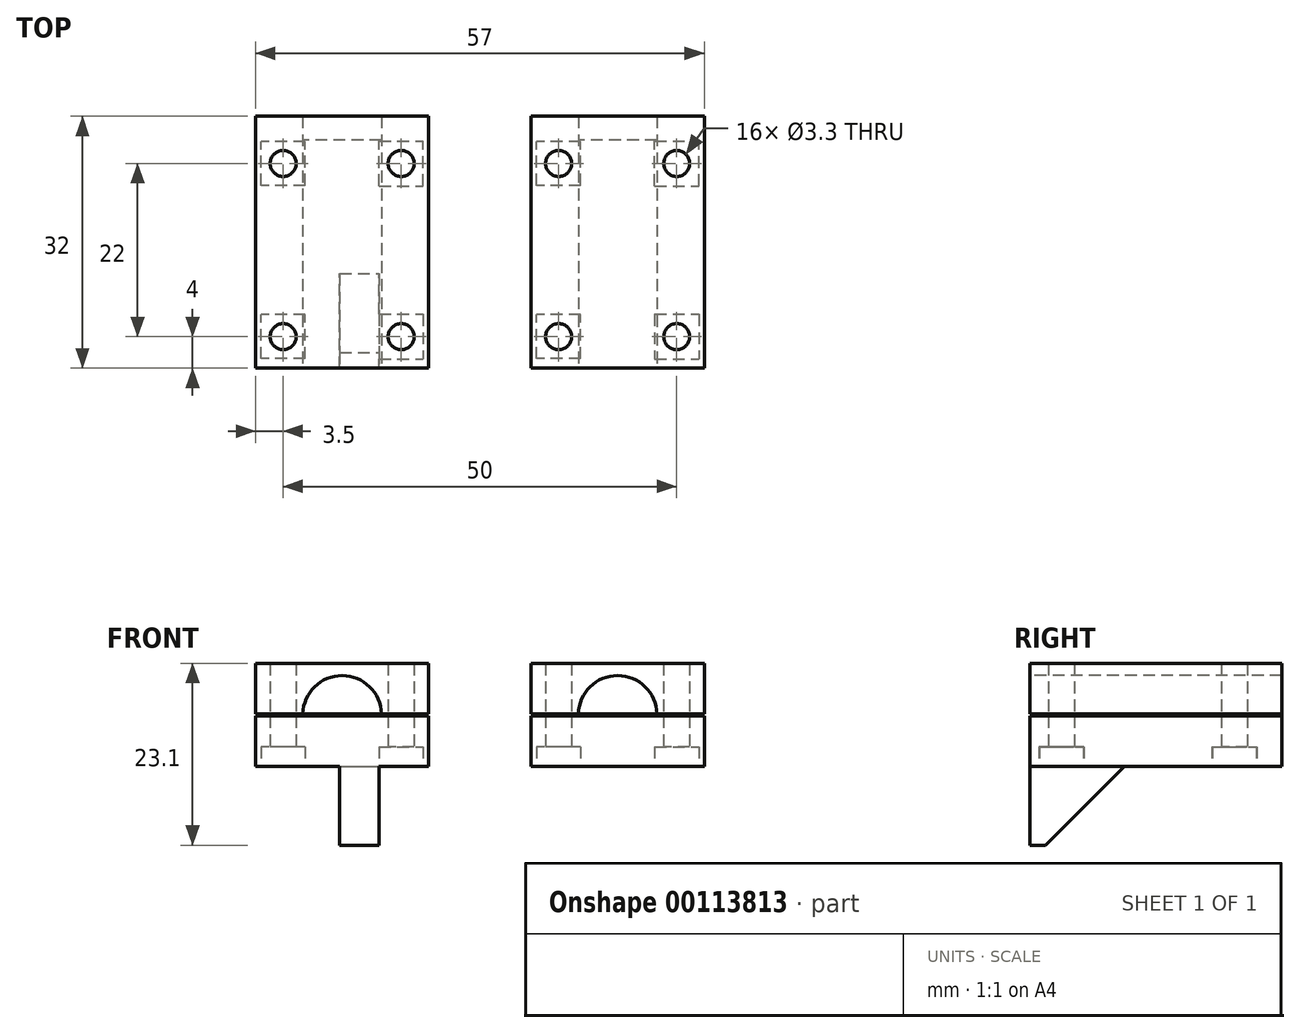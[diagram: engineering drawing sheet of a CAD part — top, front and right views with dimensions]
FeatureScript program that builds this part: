
annotation { "Feature Type Name" : "Feature", "Feature Type Description" : "" }
export const myFeature = defineFeature(function(context is Context, id is Id, definition is map)
    precondition{}
    {
        {
            var Q0;
            Q0=qCreatedBy(makeId("Top.planeOp"),FACE);
            var sketch = newSketch(context, id + "F0", { "sketchPlane" : qUnion([Q0])});
            skLineSegment(sketch, "E0.bottom", {"start": v(0, 0) * mm, "end": v(22, 0) * mm});
            skLineSegment(sketch, "E0.top", {"start": v(0, -32) * mm, "end": v(22, -32) * mm});
            skLineSegment(sketch, "E0.left", {"start": v(0, 0) * mm, "end": v(0, -32) * mm});
            skLineSegment(sketch, "E0.right", {"start": v(22, 0) * mm, "end": v(22, -32) * mm});
            skPoint(sketch, "E1", {"position": v(3.5, -28) * mm});
            skPoint(sketch, "E2", {"position": v(18.5, -28) * mm});
            skPoint(sketch, "E3", {"position": v(18.5, -6) * mm});
            skPoint(sketch, "E4", {"position": v(3.5, -6) * mm});
            skLineSegment(sketch, "E5", {"start": v(11, 0) * mm, "end": v(11, -32) * mm, "construction": true});
            skLineSegment(sketch, "E6.bottom", {"start": v(6.3, -8.8) * mm, "end": v(0.7, -8.8) * mm});
            skLineSegment(sketch, "E6.top", {"start": v(6.3, -3.2) * mm, "end": v(0.7, -3.2) * mm});
            skLineSegment(sketch, "E6.left", {"start": v(6.3, -8.8) * mm, "end": v(6.3, -3.2) * mm});
            skLineSegment(sketch, "E6.right", {"start": v(0.7, -8.8) * mm, "end": v(0.7, -3.2) * mm});
            skLineSegment(sketch, "E7.bottom", {"start": v(6.3, -30.8) * mm, "end": v(0.7, -30.8) * mm});
            skLineSegment(sketch, "E7.top", {"start": v(6.3, -25.2) * mm, "end": v(0.7, -25.2) * mm});
            skLineSegment(sketch, "E7.left", {"start": v(6.3, -30.8) * mm, "end": v(6.3, -25.2) * mm});
            skLineSegment(sketch, "E7.right", {"start": v(0.7, -30.8) * mm, "end": v(0.7, -25.2) * mm});
            skLineSegment(sketch, "E8.bottom", {"start": v(15.7, -25.14) * mm, "end": v(21.3, -25.14) * mm});
            skLineSegment(sketch, "E8.top", {"start": v(15.7, -30.86) * mm, "end": v(21.3, -30.86) * mm});
            skLineSegment(sketch, "E8.left", {"start": v(15.7, -25.14) * mm, "end": v(15.7, -30.86) * mm});
            skLineSegment(sketch, "E8.right", {"start": v(21.3, -25.14) * mm, "end": v(21.3, -30.86) * mm});
            skLineSegment(sketch, "E9.bottom", {"start": v(15.7, -8.86) * mm, "end": v(21.3, -8.86) * mm});
            skLineSegment(sketch, "E9.top", {"start": v(15.7, -3.14) * mm, "end": v(21.3, -3.14) * mm});
            skLineSegment(sketch, "E9.left", {"start": v(15.7, -8.86) * mm, "end": v(15.7, -3.14) * mm});
            skLineSegment(sketch, "E9.right", {"start": v(21.3, -8.86) * mm, "end": v(21.3, -3.14) * mm});
            skSolve(sketch);
        }
        {
            var Q0;
            Q0 = qSketchRegion(id + "F0", true);
            var Q1;
            Q1=makeQuery(id+"F0.imprint","IMPRINT",FACE,{"disambiguationData":[TD([[makeQuery(id+"F0.imprint","IMPRINT",EDGE,{"derivedFrom":sQuery(id+"F0.wireOp",EDGE,"E6.bottom")}),-1.0]])]});
            var Q2;
            Q2=makeQuery(id+"F0.imprint","IMPRINT",FACE,{"disambiguationData":[TD([[makeQuery(id+"F0.imprint","IMPRINT",EDGE,{"derivedFrom":sQuery(id+"F0.wireOp",EDGE,"E9.bottom")}),1.0]])]});
            var Q3;
            Q3=makeQuery(id+"F0.imprint","IMPRINT",FACE,{"disambiguationData":[TD([[makeQuery(id+"F0.imprint","IMPRINT",EDGE,{"derivedFrom":sQuery(id+"F0.wireOp",EDGE,"E8.bottom")}),-1.0]])]});
            var Q4;
            Q4=makeQuery(id+"F0.imprint","IMPRINT",FACE,{"disambiguationData":[TD([[makeQuery(id+"F0.imprint","IMPRINT",EDGE,{"derivedFrom":sQuery(id+"F0.wireOp",EDGE,"E7.bottom")}),-1.0]])]});
            extrude(context, id + "F1", {"entities" : qUnion([Q0, Q1, Q2, Q3, Q4]), "depth" : 13.1 * mm});
        }
        {
            var Q0;
            Q0=makeQuery(id+"F0.imprint","IMPRINT",FACE,{"disambiguationData":[TD([[makeQuery(id+"F0.imprint","IMPRINT",EDGE,{"derivedFrom":sQuery(id+"F0.wireOp",EDGE,"E7.bottom")}),-1.0]])]});
            var Q1;
            Q1=makeQuery(id+"F0.imprint","IMPRINT",FACE,{"disambiguationData":[TD([[makeQuery(id+"F0.imprint","IMPRINT",EDGE,{"derivedFrom":sQuery(id+"F0.wireOp",EDGE,"E8.bottom")}),-1.0]])]});
            var Q2;
            Q2=makeQuery(id+"F0.imprint","IMPRINT",FACE,{"disambiguationData":[TD([[makeQuery(id+"F0.imprint","IMPRINT",EDGE,{"derivedFrom":sQuery(id+"F0.wireOp",EDGE,"E6.bottom")}),-1.0]])]});
            var Q3;
            Q3=makeQuery(id+"F0.imprint","IMPRINT",FACE,{"disambiguationData":[TD([[makeQuery(id+"F0.imprint","IMPRINT",EDGE,{"derivedFrom":sQuery(id+"F0.wireOp",EDGE,"E9.bottom")}),1.0]])]});
            extrude(context, id + "F2", {"entities" : qUnion([Q0, Q1, Q2, Q3]), "operationType" : NewBodyOperationType.REMOVE, "depth" : 2.5 * mm});
        }
        {
            var Q0;
            Q0=sQuery(id+"F0.wireOp",VERTEX,"E1");
            var Q1;
            Q1=sQuery(id+"F0.wireOp",VERTEX,"E2");
            var Q2;
            Q2=sQuery(id+"F0.wireOp",VERTEX,"E3");
            var Q3;
            Q3=sQuery(id+"F0.wireOp",VERTEX,"E4");
            var Q4;
            Q4=makeQuery(id+"F1.opExtrude","SWEPT_BODY",BODY,{"disambiguationData":[OSD([sQuery(id+"F0.wireOp",EDGE,"E0.bottom"),sQuery(id+"F0.wireOp",EDGE,"E0.top"),sQuery(id+"F0.wireOp",EDGE,"E0.left"),sQuery(id+"F0.wireOp",EDGE,"E0.right")])]});
            hole(context, id + "F3", {"style" : HoleStyle.SIMPLE, "endStyle" : HoleEndStyle.THROUGH, "oppositeDirection" : true, "holeDiameter" : 3.3 * mm, "startFromSketch" : true, "locations" : qUnion([Q0, Q1, Q2, Q3]), "scope" : qUnion([Q4]), "isTappedThrough" : true});
        }
        {
            var Q0;
            Q0=makeQuery(id+"F1.opExtrude","SWEPT_FACE",FACE,{"disambiguationData":[OSD([sQuery(id+"F0.wireOp",EDGE,"E0.top")])]});
            var sketch = newSketch(context, id + "F4", { "sketchPlane" : qUnion([Q0])});
            skLineSegment(sketch, "E10", {"start": v(11, 13.1) * mm, "end": v(11, 0) * mm, "construction": true});
            skLineSegment(sketch, "E11", {"start": v(0, 6.55) * mm, "end": v(22, 6.55) * mm, "construction": true});
            skPoint(sketch, "E12", {"position": v(11, 6.55) * mm});
            skCircle(sketch, "E13", {"center": v(11, 6.55) * mm, "radius": 5 * mm});
            skLineSegment(sketch, "E14.bottom", {"start": v(22, 6.4) * mm, "end": v(0, 6.4) * mm});
            skLineSegment(sketch, "E14.top", {"start": v(22, 6.7) * mm, "end": v(0, 6.7) * mm});
            skLineSegment(sketch, "E14.left", {"start": v(22, 6.4) * mm, "end": v(22, 6.7) * mm});
            skLineSegment(sketch, "E14.right", {"start": v(0, 6.4) * mm, "end": v(0, 6.7) * mm});
            skSolve(sketch);
        }
        {
            var Q0;
            Q0=makeQuery(id+"F4.imprint","IMPRINT",FACE,{"disambiguationData":[TD([[makeQuery(id+"F4.imprint","IMPRINT",EDGE,{"derivedFrom":sQuery(id+"F4.wireOp",EDGE,"E13")}),1.0]])]});
            var Q1;
            {var subQ0=sQuery(id+"F4.wireOp",EDGE,"E14.top");var subQ1=sQuery(id+"F4.wireOp",EDGE,"E13");var subQ2=makeQuery(id+"F4.imprint","INTERSECT",VERTEX,{"disambiguationData":[OD(0.0)],"derivedFrom":[subQ1,subQ0]});Q1=makeQuery(id+"F4.imprint","IMPRINT",FACE,{"disambiguationData":[TD([[makeQuery(id+"F4.imprint","IMPRINT",EDGE,{"disambiguationData":[TD([[subQ2,1.0]])],"derivedFrom":subQ1}),1.0]])]});}
            var Q2;
            {var subQ0=sQuery(id+"F4.wireOp",EDGE,"E14.bottom");var subQ1=sQuery(id+"F4.wireOp",EDGE,"E13");var subQ2=makeQuery(id+"F4.imprint","INTERSECT",VERTEX,{"disambiguationData":[OD(0.0)],"derivedFrom":[subQ1,subQ0]});Q2=makeQuery(id+"F4.imprint","IMPRINT",FACE,{"disambiguationData":[TD([[makeQuery(id+"F4.imprint","IMPRINT",EDGE,{"disambiguationData":[TD([[subQ2,-1.0]])],"derivedFrom":subQ1}),1.0]])]});}
            extrude(context, id + "F5", {"entities" : qUnion([Q0, Q1, Q2]), "operationType" : NewBodyOperationType.REMOVE, "oppositeDirection" : true, "depth" : 29 * mm});
        }
        {
            var Q0;
            {var subQ5=sQuery(id+"F4.wireOp",EDGE,"E14.right");Q0=makeQuery(id+"F4.imprint","IMPRINT",FACE,{"disambiguationData":[TD([[makeQuery(id+"F4.imprint","IMPRINT",EDGE,{"derivedFrom":subQ5}),1.0]])]});}
            var Q1;
            {var subQ5=sQuery(id+"F4.wireOp",EDGE,"E14.left");Q1=makeQuery(id+"F4.imprint","IMPRINT",FACE,{"disambiguationData":[TD([[makeQuery(id+"F4.imprint","IMPRINT",EDGE,{"derivedFrom":subQ5}),-1.0]])]});}
            var Q2;
            {var subQ0=sQuery(id+"F4.wireOp",EDGE,"E14.top");var subQ1=sQuery(id+"F4.wireOp",EDGE,"E13");var subQ2=makeQuery(id+"F4.imprint","INTERSECT",VERTEX,{"disambiguationData":[OD(0.0)],"derivedFrom":[subQ1,subQ0]});Q2=makeQuery(id+"F4.imprint","IMPRINT",FACE,{"disambiguationData":[TD([[makeQuery(id+"F4.imprint","IMPRINT",EDGE,{"disambiguationData":[TD([[subQ2,-1.0]])],"derivedFrom":subQ1}),1.0]])]});}
            extrude(context, id + "F6", {"entities" : qUnion([Q0, Q1, Q2]), "operationType" : NewBodyOperationType.REMOVE, "endBound" : BoundingType.THROUGH_ALL, "oppositeDirection" : true, "depth" : 25 * mm});
        }
        {
            var Q0;
            Q0=makeQuery(id+"F6.boolean.opBoolean","SPLIT",BODY,{"disambiguationData":[OD(0.0)],"derivedFrom":makeQuery(id+"F1.opExtrude","SWEPT_BODY",BODY,{"disambiguationData":[OSD([sQuery(id+"F0.wireOp",EDGE,"E0.bottom"),sQuery(id+"F0.wireOp",EDGE,"E0.top"),sQuery(id+"F0.wireOp",EDGE,"E0.left"),sQuery(id+"F0.wireOp",EDGE,"E0.right")])]})});
            transform(context, id + "F7", {"entities" : qUnion([Q0]), "transformType" : TransformType.TRANSLATION_3D, "dx" : -35 * mm, "dy" : 0 * mm, "dz" : 0 * mm, "makeCopy" : true});
        }
        {
            var Q0;
            Q0=makeQuery(id+"F7.opPattern","COPY",FACE,{"derivedFrom":makeQuery(id+"F2.boolean.opBoolean","COPY",FACE,{"derivedFrom":makeQuery(id+"F2.opExtrude","SWEPT_FACE",FACE,{"disambiguationData":[OSD([sQuery(id+"F0.wireOp",EDGE,"E8.left")])]})}),"instanceName":"1"});
            var sketch = newSketch(context, id + "F8", { "sketchPlane" : qUnion([Q0])});
            skLineSegment(sketch, "E15.0", {"start": v(-25.14, 0) * mm, "end": v(-30.86, 0) * mm});
            skPoint(sketch, "E16.0", {"position": v(-32, 0) * mm});
            skLineSegment(sketch, "E17", {"start": v(-32, 0) * mm, "end": v(-20, 0) * mm});
            skLineSegment(sketch, "E18", {"start": v(-20, 0) * mm, "end": v(-30, -10) * mm});
            skLineSegment(sketch, "E19", {"start": v(-30, -10) * mm, "end": v(-32, -10) * mm});
            skLineSegment(sketch, "E20", {"start": v(-32, -10) * mm, "end": v(-32, 0) * mm});
            skSolve(sketch);
        }
        {
            var Q0;
            Q0 = qSketchRegion(id + "F8", true);
            extrude(context, id + "F9", {"entities" : qUnion([Q0]), "operationType" : NewBodyOperationType.ADD, "oppositeDirection" : true, "depth" : 5 * mm});
        }
    });
